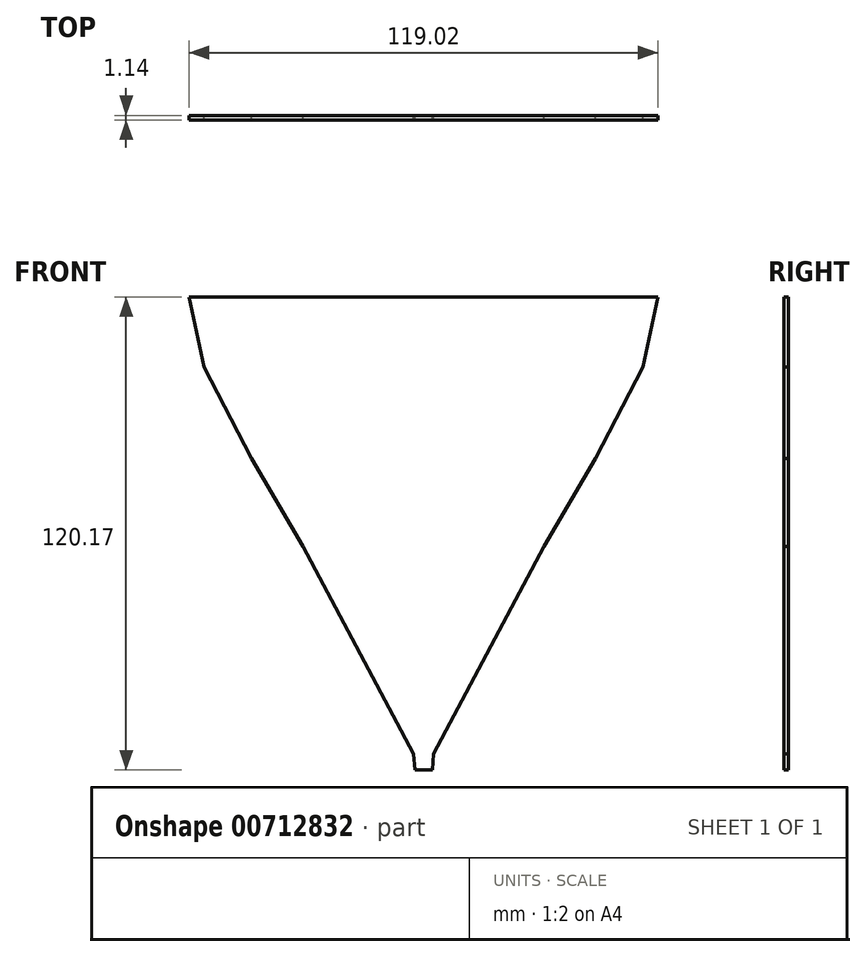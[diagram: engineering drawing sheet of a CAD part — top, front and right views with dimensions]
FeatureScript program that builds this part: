
annotation { "Feature Type Name" : "Feature", "Feature Type Description" : "" }
export const myFeature = defineFeature(function(context is Context, id is Id, definition is map)
    precondition{}
    {
        {
            var Q0;
            Q0=qCreatedBy(makeId("Front.planeOp"),FACE);
            var sketch = newSketch(context, id + "F0", { "sketchPlane" : qUnion([Q0])});
            skLineSegment(sketch, "E0", {"start": v(2.22, 29.69) * mm, "end": v(2.54, 33.81) * mm});
            skLineSegment(sketch, "E1", {"start": v(59.51, 149.86) * mm, "end": v(55.72, 132.08) * mm});
            skLineSegment(sketch, "E2", {"start": v(55.72, 132.08) * mm, "end": v(43.66, 108.9) * mm});
            skLineSegment(sketch, "E3", {"start": v(43.66, 108.9) * mm, "end": v(30.64, 86.52) * mm});
            skLineSegment(sketch, "E4", {"start": v(30.64, 86.52) * mm, "end": v(2.54, 33.81) * mm});
            skLineSegment(sketch, "E5.MirrorCS", {"start": v(-2.22, 29.69) * mm, "end": v(-2.54, 33.81) * mm});
            skLineSegment(sketch, "E6.MirrorCS", {"start": v(-59.51, 149.86) * mm, "end": v(-55.72, 132.08) * mm});
            skLineSegment(sketch, "E7.MirrorCS", {"start": v(-43.66, 108.9) * mm, "end": v(-30.64, 86.52) * mm});
            skLineSegment(sketch, "E8.MirrorCS", {"start": v(-55.72, 132.08) * mm, "end": v(-43.66, 108.9) * mm});
            skLineSegment(sketch, "E9.MirrorCS", {"start": v(-30.64, 86.52) * mm, "end": v(-2.54, 33.81) * mm});
            skLineSegment(sketch, "E10", {"start": v(-59.51, 149.86) * mm, "end": v(59.51, 149.86) * mm});
            skLineSegment(sketch, "E11", {"start": v(-2.22, 29.69) * mm, "end": v(2.22, 29.69) * mm});
            skSolve(sketch);
        }
        {
            var Q0;
            Q0=makeQuery(id+"F0.imprint","IMPRINT",FACE,{"disambiguationData":[TD([[makeQuery(id+"F0.imprint","IMPRINT",EDGE,{"derivedFrom":sQuery(id+"F0.wireOp",EDGE,"E0")}),1.0]])]});
            extrude(context, id + "F1", {"entities" : qUnion([Q0]), "endBound" : BoundingType.SYMMETRIC, "depth" : 1.14 * mm, "offsetDistance" : 25.4 * mm});
        }
    });
